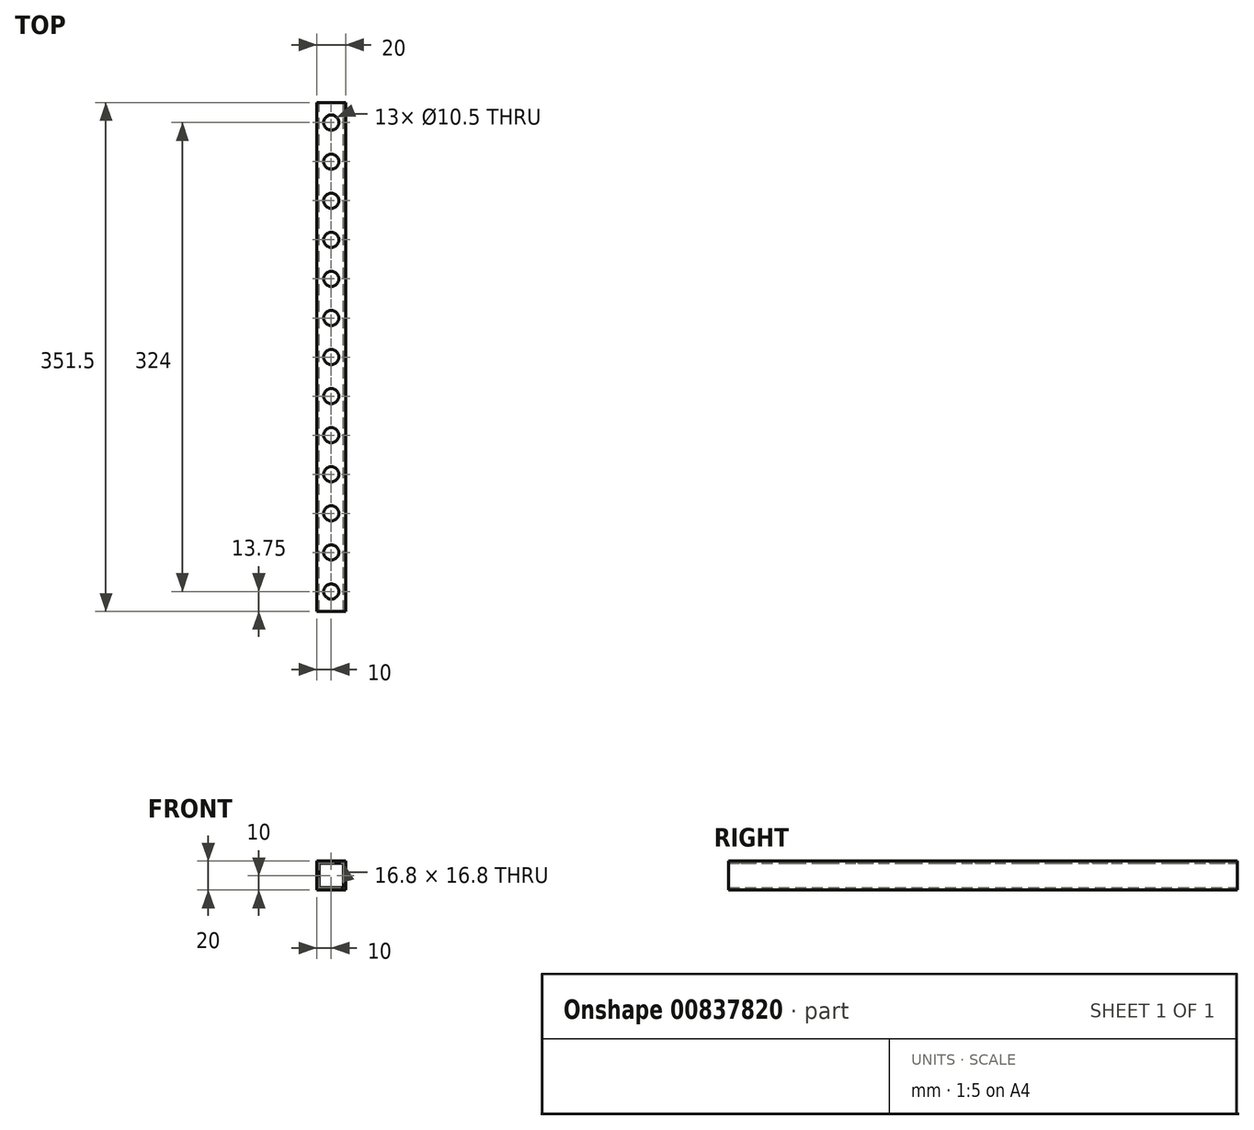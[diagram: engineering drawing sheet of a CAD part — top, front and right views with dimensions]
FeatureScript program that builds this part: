
annotation { "Feature Type Name" : "Feature", "Feature Type Description" : "" }
export const myFeature = defineFeature(function(context is Context, id is Id, definition is map)
    precondition{}
    {
        {
            var Q0;
            Q0=qCreatedBy(makeId("Front.planeOp"),FACE);
            var sketch = newSketch(context, id + "F0", { "sketchPlane" : qUnion([Q0])});
            skLineSegment(sketch, "E0.bottom", {"start": v(0, 0) * mm, "end": v(20, 0) * mm});
            skLineSegment(sketch, "E0.top", {"start": v(0, -20) * mm, "end": v(20, -20) * mm});
            skLineSegment(sketch, "E0.left", {"start": v(0, 0) * mm, "end": v(0, -20) * mm});
            skLineSegment(sketch, "E0.right", {"start": v(20, 0) * mm, "end": v(20, -20) * mm});
            skLineSegment(sketch, "E1.0", {"start": v(1.6, -1.6) * mm, "end": v(18.4, -1.6) * mm});
            skLineSegment(sketch, "E1.1", {"start": v(1.6, -1.6) * mm, "end": v(1.6, -18.4) * mm});
            skLineSegment(sketch, "E1.2", {"start": v(1.6, -18.4) * mm, "end": v(18.4, -18.4) * mm});
            skLineSegment(sketch, "E1.3", {"start": v(18.4, -1.6) * mm, "end": v(18.4, -18.4) * mm});
            skSolve(sketch);
        }
        {
            var Q0;
            Q0=makeQuery(id+"F0.imprint","IMPRINT",FACE,{"disambiguationData":[TD([[makeQuery(id+"F0.imprint","IMPRINT",EDGE,{"derivedFrom":sQuery(id+"F0.wireOp",EDGE,"E0.bottom")}),-1.0]])]});
            extrude(context, id + "F1", {"entities" : qUnion([Q0]), "depth" : (345 + 6.28 + 0.22) * mm, "offsetDistance" : 25 * mm});
        }
        {
            var Q0;
            Q0=makeQuery(id+"F1.opExtrude","SWEPT_FACE",FACE,{"disambiguationData":[OSD([sQuery(id+"F0.wireOp",EDGE,"E0.bottom")])]});
            var sketch = newSketch(context, id + "F2", { "sketchPlane" : qUnion([Q0])});
            skCircle(sketch, "E2", {"center": v(10, -13.75) * mm, "radius": 5.25 * mm});
            skPoint(sketch, "E2.centerSnap0", {"position": v(10, 0) * mm});
            skCircle(sketch, "E3.0.1.0", {"center": v(10, -40.75) * mm, "radius": 5.25 * mm});
            skCircle(sketch, "E3.0.2.0", {"center": v(10, -67.75) * mm, "radius": 5.25 * mm});
            skCircle(sketch, "E3.0.3.0", {"center": v(10, -94.75) * mm, "radius": 5.25 * mm});
            skCircle(sketch, "E3.0.4.0", {"center": v(10, -121.75) * mm, "radius": 5.25 * mm});
            skCircle(sketch, "E3.0.5.0", {"center": v(10, -148.75) * mm, "radius": 5.25 * mm});
            skCircle(sketch, "E3.0.6.0", {"center": v(10, -175.75) * mm, "radius": 5.25 * mm});
            skCircle(sketch, "E3.0.7.0", {"center": v(10, -202.75) * mm, "radius": 5.25 * mm});
            skCircle(sketch, "E3.0.8.0", {"center": v(10, -229.75) * mm, "radius": 5.25 * mm});
            skCircle(sketch, "E3.0.9.0", {"center": v(10, -256.75) * mm, "radius": 5.25 * mm});
            skCircle(sketch, "E3.0.10.0", {"center": v(10, -283.75) * mm, "radius": 5.25 * mm});
            skCircle(sketch, "E3.0.11.0", {"center": v(10, -310.75) * mm, "radius": 5.25 * mm});
            skLineSegment(sketch, "E3.direction1", {"start": v(10, -13.75) * mm, "end": v(35, -13.75) * mm, "construction": true});
            skLineSegment(sketch, "E3.direction2", {"start": v(10, -13.75) * mm, "end": v(10, -40.75) * mm, "construction": true});
            skCircle(sketch, "E4.0.0.12", {"center": v(10, -337.75) * mm, "radius": 5.25 * mm});
            skSolve(sketch);
        }
        {
            var Q0;
            Q0=makeQuery(id+"F2.imprint","IMPRINT",FACE,{"disambiguationData":[TD([[makeQuery(id+"F2.imprint","IMPRINT",EDGE,{"derivedFrom":sQuery(id+"F2.wireOp",EDGE,"E3.0.13.0")}),1.0]])]});
            var Q1;
            Q1=makeQuery(id+"F2.imprint","IMPRINT",FACE,{"disambiguationData":[TD([[makeQuery(id+"F2.imprint","IMPRINT",EDGE,{"derivedFrom":sQuery(id+"F2.wireOp",EDGE,"E3.0.12.0")}),1.0]])]});
            var Q2;
            Q2=makeQuery(id+"F2.imprint","IMPRINT",FACE,{"disambiguationData":[TD([[makeQuery(id+"F2.imprint","IMPRINT",EDGE,{"derivedFrom":sQuery(id+"F2.wireOp",EDGE,"E3.0.11.0")}),1.0]])]});
            var Q3;
            Q3=makeQuery(id+"F2.imprint","IMPRINT",FACE,{"disambiguationData":[TD([[makeQuery(id+"F2.imprint","IMPRINT",EDGE,{"derivedFrom":sQuery(id+"F2.wireOp",EDGE,"E3.0.10.0")}),1.0]])]});
            var Q4;
            Q4=makeQuery(id+"F2.imprint","IMPRINT",FACE,{"disambiguationData":[TD([[makeQuery(id+"F2.imprint","IMPRINT",EDGE,{"derivedFrom":sQuery(id+"F2.wireOp",EDGE,"E3.0.9.0")}),1.0]])]});
            var Q5;
            Q5=makeQuery(id+"F2.imprint","IMPRINT",FACE,{"disambiguationData":[TD([[makeQuery(id+"F2.imprint","IMPRINT",EDGE,{"derivedFrom":sQuery(id+"F2.wireOp",EDGE,"E3.0.8.0")}),1.0]])]});
            var Q6;
            Q6=makeQuery(id+"F2.imprint","IMPRINT",FACE,{"disambiguationData":[TD([[makeQuery(id+"F2.imprint","IMPRINT",EDGE,{"derivedFrom":sQuery(id+"F2.wireOp",EDGE,"E3.0.7.0")}),1.0]])]});
            var Q7;
            Q7=makeQuery(id+"F2.imprint","IMPRINT",FACE,{"disambiguationData":[TD([[makeQuery(id+"F2.imprint","IMPRINT",EDGE,{"derivedFrom":sQuery(id+"F2.wireOp",EDGE,"E3.0.6.0")}),1.0]])]});
            var Q8;
            Q8=makeQuery(id+"F2.imprint","IMPRINT",FACE,{"disambiguationData":[TD([[makeQuery(id+"F2.imprint","IMPRINT",EDGE,{"derivedFrom":sQuery(id+"F2.wireOp",EDGE,"E3.0.5.0")}),1.0]])]});
            var Q9;
            Q9=makeQuery(id+"F2.imprint","IMPRINT",FACE,{"disambiguationData":[TD([[makeQuery(id+"F2.imprint","IMPRINT",EDGE,{"derivedFrom":sQuery(id+"F2.wireOp",EDGE,"E3.0.4.0")}),1.0]])]});
            var Q10;
            Q10=makeQuery(id+"F2.imprint","IMPRINT",FACE,{"disambiguationData":[TD([[makeQuery(id+"F2.imprint","IMPRINT",EDGE,{"derivedFrom":sQuery(id+"F2.wireOp",EDGE,"E3.0.3.0")}),1.0]])]});
            var Q11;
            Q11=makeQuery(id+"F2.imprint","IMPRINT",FACE,{"disambiguationData":[TD([[makeQuery(id+"F2.imprint","IMPRINT",EDGE,{"derivedFrom":sQuery(id+"F2.wireOp",EDGE,"E3.0.2.0")}),1.0]])]});
            var Q12;
            Q12=makeQuery(id+"F2.imprint","IMPRINT",FACE,{"disambiguationData":[TD([[makeQuery(id+"F2.imprint","IMPRINT",EDGE,{"derivedFrom":sQuery(id+"F2.wireOp",EDGE,"E3.0.1.0")}),1.0]])]});
            var Q13;
            Q13=makeQuery(id+"F2.imprint","IMPRINT",FACE,{"disambiguationData":[TD([[makeQuery(id+"F2.imprint","IMPRINT",EDGE,{"derivedFrom":sQuery(id+"F2.wireOp",EDGE,"E2")}),1.0]])]});
            var Q14;
            Q14=makeQuery(id+"F2.imprint","IMPRINT",FACE,{"disambiguationData":[TD([[makeQuery(id+"F2.imprint","IMPRINT",EDGE,{"derivedFrom":sQuery(id+"F2.wireOp",EDGE,"E4.0.0.12")}),1.0]])]});
            extrude(context, id + "F3", {"entities" : qUnion([Q0, Q1, Q2, Q3, Q4, Q5, Q6, Q7, Q8, Q9, Q10, Q11, Q12, Q13, Q14]), "operationType" : NewBodyOperationType.REMOVE, "oppositeDirection" : true, "depth" : 5 * mm, "offsetDistance" : 25 * mm});
        }
    });
